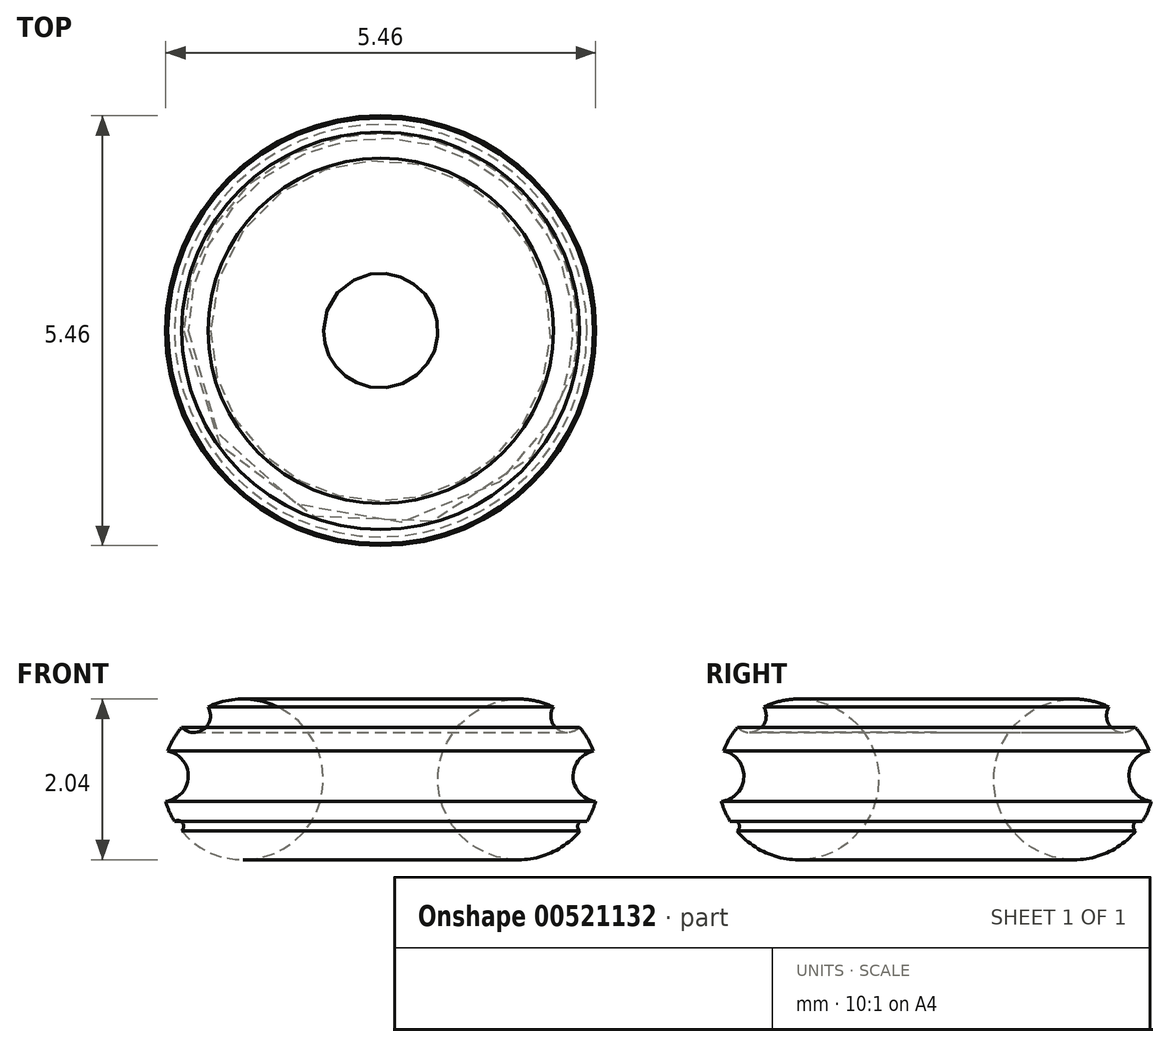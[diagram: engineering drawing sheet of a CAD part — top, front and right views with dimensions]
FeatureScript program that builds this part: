
annotation { "Feature Type Name" : "Feature", "Feature Type Description" : "" }
export const myFeature = defineFeature(function(context is Context, id is Id, definition is map)
    precondition{}
    {
        {
            var Q0;
            Q0=qCreatedBy(makeId("Front.planeOp"),FACE);
            var sketch = newSketch(context, id + "F0", { "sketchPlane" : qUnion([Q0])});
            skArc(sketch, "E0", {"start": v(0.87, -0.53) * mm, "mid": v(0.93, -0.41) * mm, "end": v(0.98, -0.28) * mm});
            skArc(sketch, "E1", {"start": v(0.44, 0.92) * mm, "mid": v(0.5, 0.64) * mm, "end": v(0.78, 0.66) * mm});
            skArc(sketch, "E2", {"start": v(0.87, -0.53) * mm, "mid": v(0.77, -0.55) * mm, "end": v(0.78, -0.66) * mm});
            skArc(sketch, "E3.trimOffspring", {"start": v(0.44, 0.92) * mm, "mid": v(-1, -0.21) * mm, "end": v(0.78, -0.66) * mm});
            skArc(sketch, "E4", {"start": v(0.95, 0.36) * mm, "mid": v(0.7, 0.03) * mm, "end": v(0.98, -0.28) * mm});
            skArc(sketch, "E5.trimOffspring", {"start": v(0.95, 0.36) * mm, "mid": v(0.88, 0.52) * mm, "end": v(0.78, 0.66) * mm});
            skLineSegment(sketch, "E6", {"start": v(-1.75, 0) * mm, "end": v(-1.75, 1.94) * mm});
            skSolve(sketch);
        }
        {
            var Q0;
            Q0=makeQuery(id+"F0.imprint","IMPRINT",FACE,{"disambiguationData":[TD([[makeQuery(id+"F0.imprint","IMPRINT",EDGE,{"derivedFrom":sQuery(id+"F0.wireOp",EDGE,"E0")}),1.0]])]});
            var Q1;
            Q1=sQuery(id+"F0.wireOp",EDGE,"E6");
            revolve(context, id + "F1", {"entities" : qUnion([Q0]), "axis" : qUnion([Q1]), "revolveType" : RevolveType.FULL});
        }
    });
